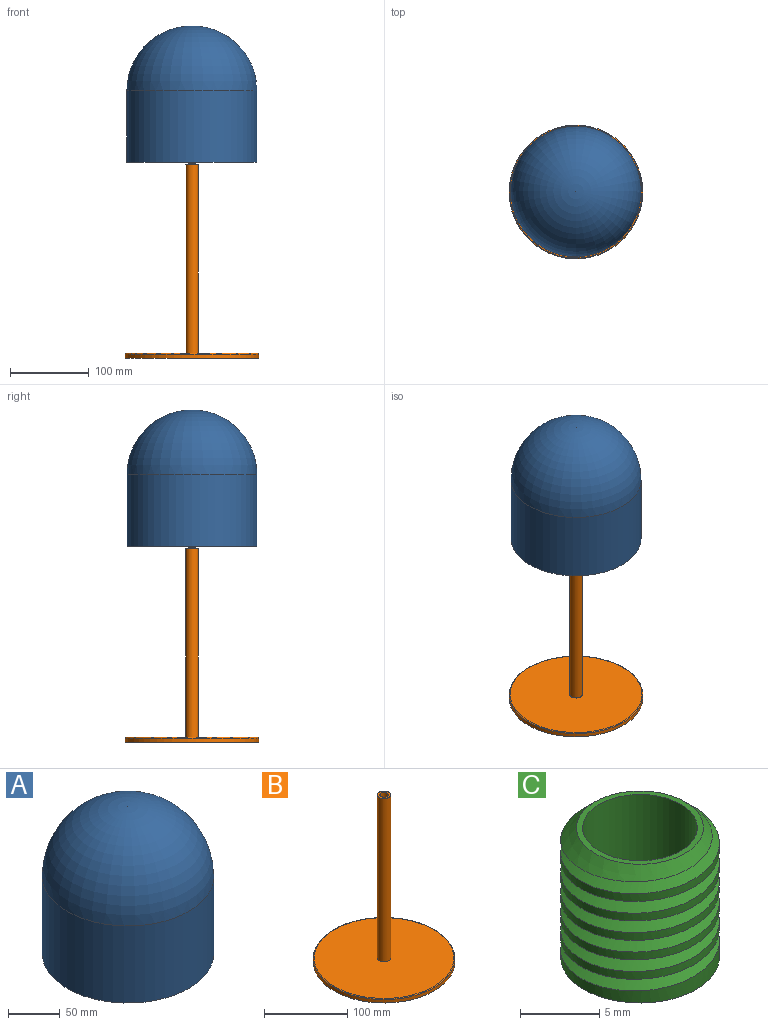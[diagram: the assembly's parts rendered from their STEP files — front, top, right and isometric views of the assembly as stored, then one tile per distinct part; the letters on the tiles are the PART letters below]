
ASSEMBLY  parts=3 mates=2
PART A: 5 faces, bbox 165.4x165.4x173.3 mm
  f0: torus R=1.09mm, axis (0,0,-1), area 38690mm2, adj f1
  f1: cylinder r=78.71mm len=157.41mm, axis (0,0,-1), area 45319.8mm2, adj f0,f2
  f2: plane 165.41x165.41mm, normal (0,0,-1), area 2028.4mm2, adj f1,f3
  f3: cylinder r=82.71mm len=165.41mm, axis (0,0,-1), area 47285.1mm2, adj f2,f4
  f4: torus R=0.45mm, axis (0,0,-1), area 42878.9mm2, adj f3
PART B: 7 faces, bbox 184x184x246 mm
  f0: cylinder r=85mm len=170mm, axis (0,0,-1), area 2670.4mm2, adj f2,f6
  f1: plane 168x168mm, normal (0,0,1), area 21966mm2, adj f3,f6
  f2: plane 170x170mm, normal (0,0,-1), area 22619.5mm2, adj f0,f5
  f3: cylinder r=8mm len=240mm, axis (0,0,-1), area 12063.7mm2, adj f1,f4
  f4: plane 16x16mm, normal (0,0,1), area 122.5mm2, adj f3,f5
  f5: cylinder r=5mm len=246mm, axis (0,0,1), area 7728.3mm2, adj f2,f4
  f6: torus R=84mm, axis (0,0,1), area 835.3mm2, adj f0,f1
PART C: 9 faces, bbox 10x11.5x10 mm
  f0: cone r=4mm half-angle=45deg, axis (0,0,-1), area 32.7mm2, adj f2,f3,f5,f7
  f1: cylinder r=3.61mm len=10mm, axis (0,0,-1), area 227.1mm2, adj f3,f4
  f2: cylinder r=5mm len=10mm, axis (0,0,-1), area 122mm2, adj f0,f4,f6,f7,f8
  f3: plane 8x8mm, normal (0,0,1), area 9.2mm2, adj f0,f1
  f4: plane 10x10mm, normal (0,0,-1), area 37.5mm2, adj f1,f2
  f5: plane 0.78x0.57mm, normal (0,-1,0), area 0.1mm2, adj f0,f7,f8
  f6: plane 0.9x0.78mm, normal (0,1,0), area 0.4mm2, adj f2,f7,f8
  f7: bspline ~11.55x10mm, area 150.6mm2, adj f0,f2,f5,f6,f8
  f8: bspline ~11.55x10mm, area 156.6mm2, adj f2,f5,f6,f7
PLACE A t=(-214.16,-50.13,137.26)mm
PLACE B t=(-214.16,-50.13,-198.05)mm
PLACE C t=(-214.16,-50.13,-198.05)mm
MATE slider B.f0 <-> C.f0  axis (0,0,1) through (-214.16,-50.13,47.95)mm
MATE planar B.f0 <-> A.f0  axis (0,0,-1) through (-214.16,-50.13,47.95)mm
